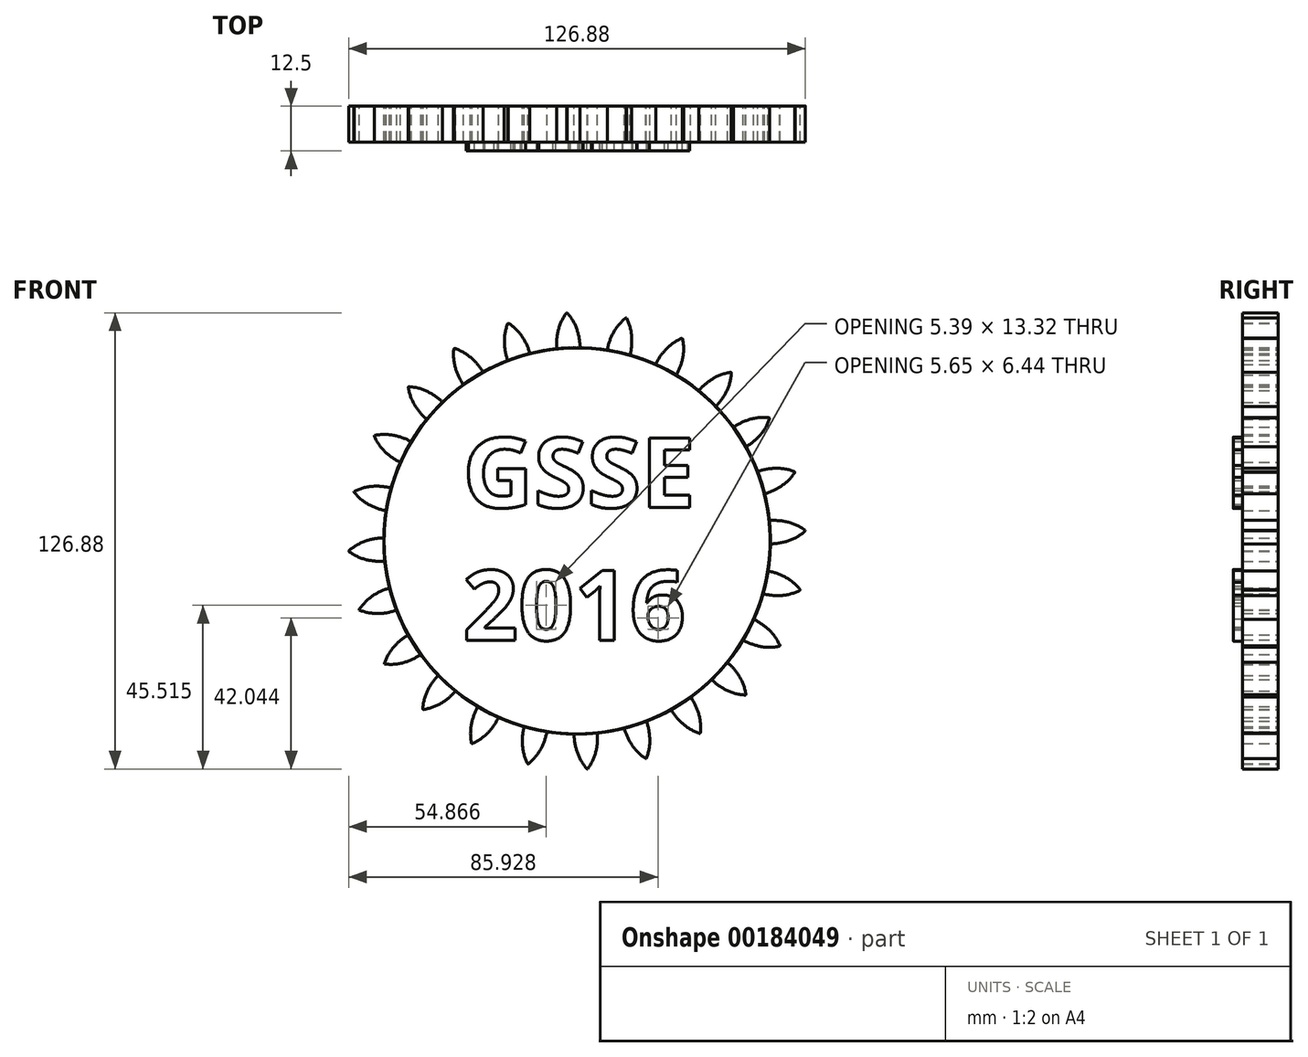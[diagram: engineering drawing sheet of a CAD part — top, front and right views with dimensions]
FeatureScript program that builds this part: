
annotation { "Feature Type Name" : "Feature", "Feature Type Description" : "" }
export const myFeature = defineFeature(function(context is Context, id is Id, definition is map)
    precondition{}
    {
        {
            var Q0;
            Q0=qCreatedBy(makeId("Front.planeOp"),FACE);
            var sketch = newSketch(context, id + "F0", { "sketchPlane" : qUnion([Q0])});
            skCircle(sketch, "E0", {"center": v(0, 0) * mm, "radius": 63.5 * mm, "construction": true});
            skCircle(sketch, "E1", {"center": v(0, 0) * mm, "radius": 58.67 * mm, "construction": true});
            skCircle(sketch, "E2", {"center": v(0, 0) * mm, "radius": 53.72 * mm});
            skLineSegment(sketch, "E3", {"start": v(0, 0) * mm, "end": v(0, 85.62) * mm, "construction": true});
            skLineSegment(sketch, "E4", {"start": v(0, 0) * mm, "end": v(-3.75, 83.5) * mm, "construction": true});
            skLineSegment(sketch, "E5", {"start": v(0, 58.67) * mm, "end": v(-71, 60.24) * mm, "construction": true});
            skLineSegment(sketch, "E6", {"start": v(0, 58.67) * mm, "end": v(-79.45, 31.72) * mm, "construction": true});
            skCircle(sketch, "E7", {"center": v(0, 58.67) * mm, "radius": 14.6 * mm, "construction": true});
            skCircle(sketch, "E8", {"center": v(0, 0) * mm, "radius": 55.56 * mm, "construction": true});
            skCircle(sketch, "E9", {"center": v(-13.78, 53.83) * mm, "radius": 14.6 * mm, "construction": true});
            skArc(sketch, "E10", {"start": v(0, 58.67) * mm, "mid": v(-1.14, 61.2) * mm, "end": v(-2.78, 63.44) * mm});
            skArc(sketch, "E11", {"start": v(0.83, 53.71) * mm, "mid": v(0.6, 56.23) * mm, "end": v(0, 58.67) * mm});
            skArc(sketch, "E12.MirrorCS", {"start": v(-5.26, 58.44) * mm, "mid": v(-4.35, 61.06) * mm, "end": v(-2.92, 63.43) * mm});
            skArc(sketch, "E13.MirrorCS", {"start": v(-5.64, 53.42) * mm, "mid": v(-5.64, 55.95) * mm, "end": v(-5.26, 58.44) * mm});
            skArc(sketch, "E14", {"start": v(-2.78, 63.44) * mm, "mid": v(-2.85, 63.44) * mm, "end": v(-2.92, 63.43) * mm});
            skArc(sketch, "E15", {"start": v(0.83, 53.71) * mm, "mid": v(-2.4, 53.61) * mm, "end": v(-5.64, 53.42) * mm, "construction": true});
            skSolve(sketch);
        }
        {
            var Q0;
            {var subQ0=sQuery(id+"F0.wireOp",EDGE,"E2");var subQ1=makeQuery(id+"F0.imprint","INTERSECT",VERTEX,{"derivedFrom":[subQ0,sQuery(id+"F0.wireOp",EDGE,"E11")]});Q0=makeQuery(id+"F0.imprint","IMPRINT",FACE,{"disambiguationData":[TD([[makeQuery(id+"F0.imprint","IMPRINT",EDGE,{"disambiguationData":[TD([[subQ1,-1.0]])],"derivedFrom":subQ0}),1.0]])]});}
            var Q1;
            Q1=makeQuery(id+"F0.imprint","IMPRINT",FACE,{"disambiguationData":[TD([[makeQuery(id+"F0.imprint","IMPRINT",EDGE,{"derivedFrom":sQuery(id+"F0.wireOp",EDGE,"E10")}),1.0]])]});
            extrude(context, id + "F1", {"entities" : qUnion([Q0, Q1]), "endBound" : BoundingType.SYMMETRIC, "depth" : 10 * mm});
        }
        {
            var Q0;
            Q0=makeQuery(id+"F1.opExtrude","SWEPT_BODY",BODY,{"disambiguationData":[OSD([sQuery(id+"F0.wireOp",EDGE,"E2"),sQuery(id+"F0.wireOp",EDGE,"E10"),sQuery(id+"F0.wireOp",EDGE,"E11"),sQuery(id+"F0.wireOp",EDGE,"E12.MirrorCS"),sQuery(id+"F0.wireOp",EDGE,"E13.MirrorCS"),sQuery(id+"F0.wireOp",EDGE,"E14")])]});
            var Q1;
            Q1=makeQuery(id+"F1.opExtrude","SWEPT_FACE",FACE,{"disambiguationData":[OSD([sQuery(id+"F0.wireOp",EDGE,"E2")])]});
            circularPattern(context, id + "F2", {"entities" : qUnion([Q0]), "axis" : qUnion([Q1]), "angle" : 15 * degree, "instanceCount" : 24});
        }
        {
            var Q0;
            Q0=makeQuery(id+"F1.opExtrude","CAP_FACE",FACE,{"disambiguationData":[OSD([sQuery(id+"F0.wireOp",EDGE,"E2"),sQuery(id+"F0.wireOp",EDGE,"E10"),sQuery(id+"F0.wireOp",EDGE,"E11"),sQuery(id+"F0.wireOp",EDGE,"E12.MirrorCS"),sQuery(id+"F0.wireOp",EDGE,"E13.MirrorCS"),sQuery(id+"F0.wireOp",EDGE,"E14")])],"isStart":false});
            var sketch = newSketch(context, id + "F3", { "sketchPlane" : qUnion([Q0])});
            skText(sketch, "E16", { "text": "GSSE\n2016", "fontName": "OpenSans-Bold.ttf"});
            const initialGuessF3  = {"E16": [-0.0318, 0.00927, 1, 0, 0.01953]};
            skSetInitialGuess(sketch, initialGuessF3);
            skSolve(sketch);
        }
        {
            var Q0;
            Q0 = qSketchRegion(id + "F3", true);
            extrude(context, id + "F4", {"entities" : qUnion([Q0]), "depth" : 2.5 * mm});
        }
    });
